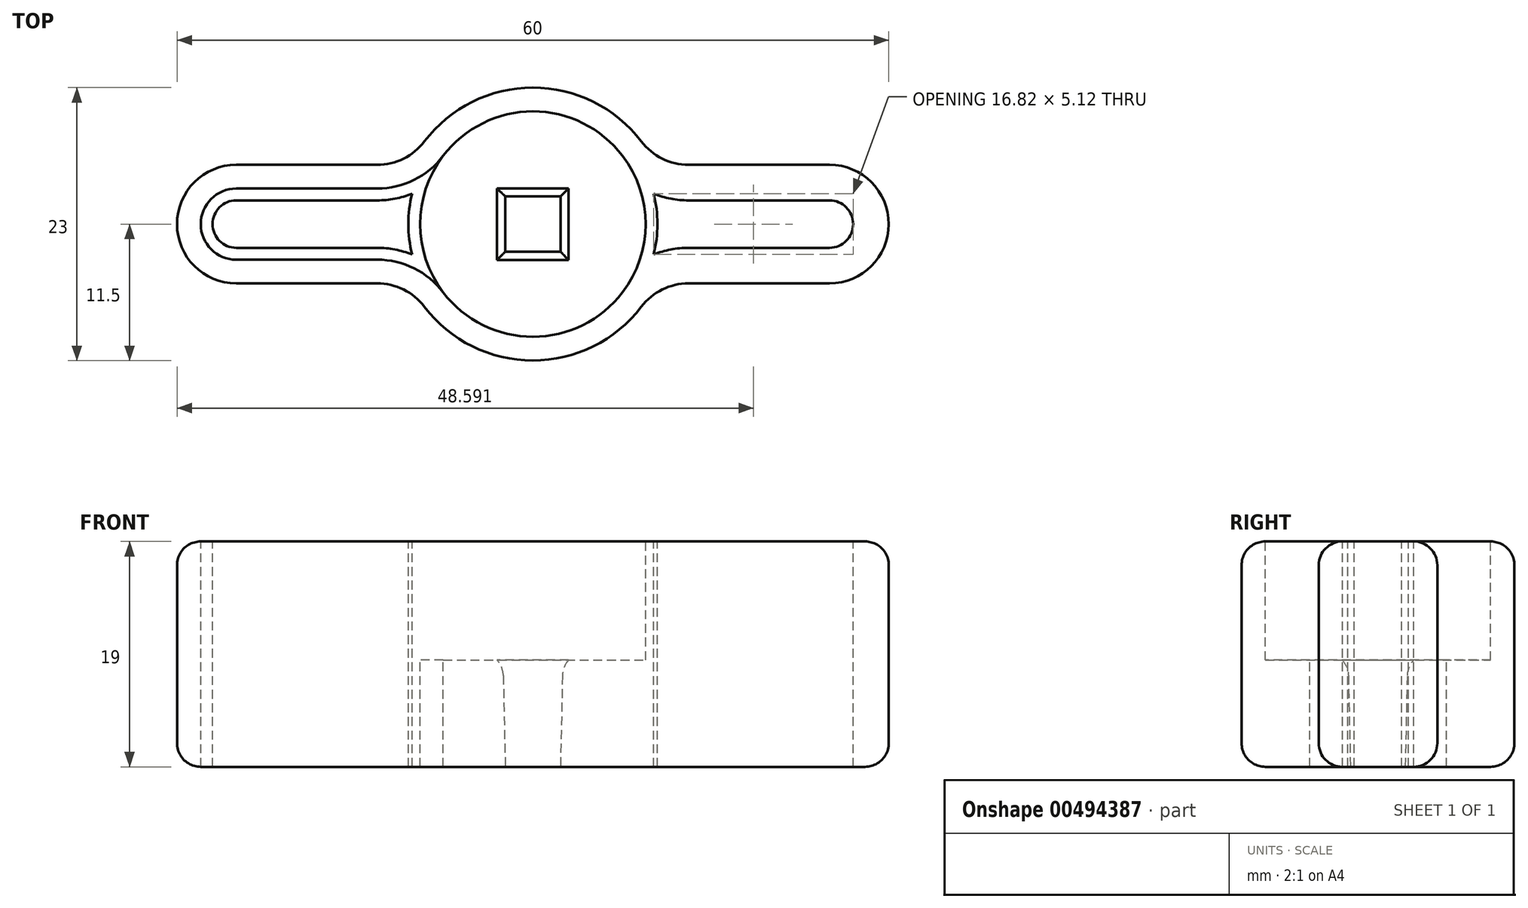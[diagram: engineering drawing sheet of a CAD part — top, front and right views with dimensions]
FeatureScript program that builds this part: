
annotation { "Feature Type Name" : "Feature", "Feature Type Description" : "" }
export const myFeature = defineFeature(function(context is Context, id is Id, definition is map)
    precondition{}
    {
        {
            var Q0;
            Q0=qCreatedBy(makeId("Top.planeOp"),FACE);
            var sketch = newSketch(context, id + "F0", { "sketchPlane" : qUnion([Q0])});
            skCircle(sketch, "E0", {"center": v(0, 0) * mm, "radius": 11.5 * mm});
            skLineSegment(sketch, "E1.bottom", {"start": v(2.32, 2.33) * mm, "end": v(-2.33, 2.33) * mm});
            skLineSegment(sketch, "E1.top", {"start": v(2.32, -2.33) * mm, "end": v(-2.33, -2.33) * mm});
            skLineSegment(sketch, "E1.left", {"start": v(2.32, 2.33) * mm, "end": v(2.32, -2.33) * mm});
            skLineSegment(sketch, "E1.right", {"start": v(-2.33, 2.33) * mm, "end": v(-2.33, -2.33) * mm});
            skLineSegment(sketch, "E2.bottom", {"start": v(30, 5) * mm, "end": v(-30, 5) * mm});
            skLineSegment(sketch, "E2.top", {"start": v(30, -5) * mm, "end": v(-30, -5) * mm});
            skLineSegment(sketch, "E2.left", {"start": v(30, 5) * mm, "end": v(30, -5) * mm});
            skLineSegment(sketch, "E2.right", {"start": v(-30, 5) * mm, "end": v(-30, -5) * mm});
            skSolve(sketch);
        }
        {
            var Q0;
            Q0=makeQuery(id+"F0.imprint","IMPRINT",FACE,{"disambiguationData":[TD([[makeQuery(id+"F0.imprint","IMPRINT",EDGE,{"derivedFrom":sQuery(id+"F0.wireOp",EDGE,"E0")}),1.0]])]});
            var Q1;
            {var subQ5=sQuery(id+"F0.wireOp",EDGE,"E2.right");Q1=makeQuery(id+"F0.imprint","IMPRINT",FACE,{"disambiguationData":[TD([[makeQuery(id+"F0.imprint","IMPRINT",EDGE,{"derivedFrom":subQ5}),1.0]])]});}
            var Q2;
            {var subQ5=sQuery(id+"F0.wireOp",EDGE,"E2.left");Q2=makeQuery(id+"F0.imprint","IMPRINT",FACE,{"disambiguationData":[TD([[makeQuery(id+"F0.imprint","IMPRINT",EDGE,{"derivedFrom":subQ5}),-1.0]])]});}
            extrude(context, id + "F1", {"entities" : qUnion([Q0, Q1, Q2]), "depth" : 19 * mm, "offsetDistance" : 25 * mm});
        }
        {
            var Q0;
            Q0=makeQuery(id+"F1.opExtrude","CAP_FACE",FACE,{"disambiguationData":[OSD([sQuery(id+"F0.wireOp",EDGE,"E0"),sQuery(id+"F0.wireOp",EDGE,"E1.bottom"),sQuery(id+"F0.wireOp",EDGE,"E1.top"),sQuery(id+"F0.wireOp",EDGE,"E1.left"),sQuery(id+"F0.wireOp",EDGE,"E1.right"),sQuery(id+"F0.wireOp",EDGE,"E2.bottom"),sQuery(id+"F0.wireOp",EDGE,"E2.top"),sQuery(id+"F0.wireOp",EDGE,"E2.left"),sQuery(id+"F0.wireOp",EDGE,"E2.right")])],"isStart":false});
            var sketch = newSketch(context, id + "F2", { "sketchPlane" : qUnion([Q0])});
            skCircle(sketch, "E3", {"center": v(0, 0) * mm, "radius": 9.5 * mm});
            skSolve(sketch);
        }
        {
            var Q0;
            Q0 = qSketchRegion(id + "F2", true);
            extrude(context, id + "F3", {"entities" : qUnion([Q0]), "operationType" : NewBodyOperationType.REMOVE, "oppositeDirection" : true, "depth" : 10 * mm, "offsetDistance" : 25 * mm});
        }
        {
            var Q0;
            Q0=makeQuery(id+"F3.boolean.opBoolean","INTERSECT",EDGE,{"derivedFrom":[makeQuery(id+"F1.opExtrude","SWEPT_FACE",FACE,{"disambiguationData":[OSD([sQuery(id+"F0.wireOp",EDGE,"E1.top")])]}),makeQuery(id+"F3.opExtrude","CAP_FACE",FACE,{"disambiguationData":[OSD([sQuery(id+"F2.wireOp",EDGE,"E3")])],"isStart":false})]});
            var Q1;
            Q1=makeQuery(id+"F3.boolean.opBoolean","INTERSECT",EDGE,{"derivedFrom":[makeQuery(id+"F1.opExtrude","SWEPT_FACE",FACE,{"disambiguationData":[OSD([sQuery(id+"F0.wireOp",EDGE,"E1.left")])]}),makeQuery(id+"F3.opExtrude","CAP_FACE",FACE,{"disambiguationData":[OSD([sQuery(id+"F2.wireOp",EDGE,"E3")])],"isStart":false})]});
            var Q2;
            Q2=makeQuery(id+"F3.boolean.opBoolean","INTERSECT",EDGE,{"derivedFrom":[makeQuery(id+"F1.opExtrude","SWEPT_FACE",FACE,{"disambiguationData":[OSD([sQuery(id+"F0.wireOp",EDGE,"E1.bottom")])]}),makeQuery(id+"F3.opExtrude","CAP_FACE",FACE,{"disambiguationData":[OSD([sQuery(id+"F2.wireOp",EDGE,"E3")])],"isStart":false})]});
            var Q3;
            Q3=makeQuery(id+"F3.boolean.opBoolean","INTERSECT",EDGE,{"derivedFrom":[makeQuery(id+"F1.opExtrude","SWEPT_FACE",FACE,{"disambiguationData":[OSD([sQuery(id+"F0.wireOp",EDGE,"E1.right")])]}),makeQuery(id+"F3.opExtrude","CAP_FACE",FACE,{"disambiguationData":[OSD([sQuery(id+"F2.wireOp",EDGE,"E3")])],"isStart":false})]});
            chamfer(context, id + "F4", {"entities" : qUnion([Q0, Q1, Q2, Q3]), "chamferType" : ChamferType.TWO_OFFSETS, "width1" : 9 * mm, "oppositeDirection" : true, "width2" : 0.2 * mm, "tangentPropagation" : true});
        }
        {
            var Q0;
            {var subQ0=sQuery(id+"F0.wireOp",EDGE,"E2.bottom");var subQ1=sQuery(id+"F0.wireOp",EDGE,"E0");Q0=makeQuery(id+"F1.opExtrude","SWEPT_EDGE",EDGE,{"disambiguationData":[OSD([subQ1,subQ0]),TDD([makeQuery(id+"F0.imprint","INTERSECT",VERTEX,{"disambiguationData":[OD(0.0)],"derivedFrom":[subQ1,subQ0]})])]});}
            var Q1;
            {var subQ0=sQuery(id+"F0.wireOp",EDGE,"E2.bottom");var subQ1=sQuery(id+"F0.wireOp",EDGE,"E0");Q1=makeQuery(id+"F1.opExtrude","SWEPT_EDGE",EDGE,{"disambiguationData":[OSD([subQ1,subQ0]),TDD([makeQuery(id+"F0.imprint","INTERSECT",VERTEX,{"disambiguationData":[OD(1.0)],"derivedFrom":[subQ1,subQ0]})])]});}
            var Q2;
            Q2=makeQuery(id+"F1.opExtrude","SWEPT_EDGE",EDGE,{"disambiguationData":[OSD([sQuery(id+"F0.wireOp",EDGE,"E2.bottom"),sQuery(id+"F0.wireOp",EDGE,"E2.right")])]});
            var Q3;
            Q3=makeQuery(id+"F1.opExtrude","SWEPT_EDGE",EDGE,{"disambiguationData":[OSD([sQuery(id+"F0.wireOp",EDGE,"E2.top"),sQuery(id+"F0.wireOp",EDGE,"E2.right")])]});
            var Q4;
            {var subQ0=sQuery(id+"F0.wireOp",EDGE,"E2.top");var subQ1=sQuery(id+"F0.wireOp",EDGE,"E0");Q4=makeQuery(id+"F1.opExtrude","SWEPT_EDGE",EDGE,{"disambiguationData":[OSD([subQ1,subQ0]),TDD([makeQuery(id+"F0.imprint","INTERSECT",VERTEX,{"disambiguationData":[OD(0.0)],"derivedFrom":[subQ1,subQ0]})])]});}
            var Q5;
            {var subQ0=sQuery(id+"F0.wireOp",EDGE,"E2.top");var subQ1=sQuery(id+"F0.wireOp",EDGE,"E0");Q5=makeQuery(id+"F1.opExtrude","SWEPT_EDGE",EDGE,{"disambiguationData":[OSD([subQ1,subQ0]),TDD([makeQuery(id+"F0.imprint","INTERSECT",VERTEX,{"disambiguationData":[OD(1.0)],"derivedFrom":[subQ1,subQ0]})])]});}
            var Q6;
            Q6=makeQuery(id+"F1.opExtrude","SWEPT_EDGE",EDGE,{"disambiguationData":[OSD([sQuery(id+"F0.wireOp",EDGE,"E2.top"),sQuery(id+"F0.wireOp",EDGE,"E2.left")])]});
            var Q7;
            Q7=makeQuery(id+"F1.opExtrude","SWEPT_EDGE",EDGE,{"disambiguationData":[OSD([sQuery(id+"F0.wireOp",EDGE,"E2.bottom"),sQuery(id+"F0.wireOp",EDGE,"E2.left")])]});
            fillet(context, id + "F5", {"entities" : qUnion([Q0, Q1, Q2, Q3, Q4, Q5, Q6, Q7]), "radius" : 5 * mm, "tangentPropagation" : true, "allowEdgeOverflow" : false});
        }
        {
            var Q0;
            {var subQ0=sQuery(id+"F0.wireOp",EDGE,"E2.bottom");Q0=makeQuery(id+"F1.opExtrude","CAP_EDGE",EDGE,{"disambiguationData":[OSD([subQ0]),TDD([makeQuery(id+"F0.imprint","IMPRINT",EDGE,{"disambiguationData":[TD([[makeQuery(id+"F0.imprint","INTERSECT",VERTEX,{"derivedFrom":[subQ0,sQuery(id+"F0.wireOp",EDGE,"E2.right")]}),1.0]])],"derivedFrom":subQ0})])],"isStart":true});}
            var Q1;
            {var subQ0=sQuery(id+"F0.wireOp",EDGE,"E2.bottom");Q1=makeQuery(id+"F1.opExtrude","CAP_EDGE",EDGE,{"disambiguationData":[OSD([subQ0]),TDD([makeQuery(id+"F0.imprint","IMPRINT",EDGE,{"disambiguationData":[TD([[makeQuery(id+"F0.imprint","INTERSECT",VERTEX,{"derivedFrom":[subQ0,sQuery(id+"F0.wireOp",EDGE,"E2.right")]}),1.0]])],"derivedFrom":subQ0})])],"isStart":false});}
            fillet(context, id + "F6", {"entities" : qUnion([Q0, Q1]), "radius" : 2 * mm, "tangentPropagation" : true, "allowEdgeOverflow" : false});
        }
        {
            var Q0;
            {var subQ0=makeQuery(id+"F3.opExtrude","CAP_FACE",FACE,{"disambiguationData":[OSD([sQuery(id+"F2.wireOp",EDGE,"E3")])],"isStart":false});Q0=makeQuery(id+"F4.opChamfer","BLEND_EDGE",EDGE,{"blendedFrom":[makeQuery(id+"F3.boolean.opBoolean","INTERSECT",EDGE,{"derivedFrom":[makeQuery(id+"F1.opExtrude","SWEPT_FACE",FACE,{"disambiguationData":[OSD([sQuery(id+"F0.wireOp",EDGE,"E1.bottom")])]}),subQ0]}),makeQuery(id+"F3.boolean.opBoolean","COPY",FACE,{"derivedFrom":subQ0})],"blendedInto":[makeQuery(id+"F3.boolean.opBoolean","COPY",FACE,{"derivedFrom":subQ0})]});}
            var Q1;
            {var subQ0=makeQuery(id+"F3.opExtrude","CAP_FACE",FACE,{"disambiguationData":[OSD([sQuery(id+"F2.wireOp",EDGE,"E3")])],"isStart":false});Q1=makeQuery(id+"F4.opChamfer","BLEND_EDGE",EDGE,{"blendedFrom":[makeQuery(id+"F3.boolean.opBoolean","INTERSECT",EDGE,{"derivedFrom":[makeQuery(id+"F1.opExtrude","SWEPT_FACE",FACE,{"disambiguationData":[OSD([sQuery(id+"F0.wireOp",EDGE,"E1.right")])]}),subQ0]}),makeQuery(id+"F3.boolean.opBoolean","COPY",FACE,{"derivedFrom":subQ0})],"blendedInto":[makeQuery(id+"F3.boolean.opBoolean","COPY",FACE,{"derivedFrom":subQ0})]});}
            var Q2;
            {var subQ0=makeQuery(id+"F3.opExtrude","CAP_FACE",FACE,{"disambiguationData":[OSD([sQuery(id+"F2.wireOp",EDGE,"E3")])],"isStart":false});Q2=makeQuery(id+"F4.opChamfer","BLEND_EDGE",EDGE,{"blendedFrom":[makeQuery(id+"F3.boolean.opBoolean","INTERSECT",EDGE,{"derivedFrom":[makeQuery(id+"F1.opExtrude","SWEPT_FACE",FACE,{"disambiguationData":[OSD([sQuery(id+"F0.wireOp",EDGE,"E1.left")])]}),subQ0]}),makeQuery(id+"F3.boolean.opBoolean","COPY",FACE,{"derivedFrom":subQ0})],"blendedInto":[makeQuery(id+"F3.boolean.opBoolean","COPY",FACE,{"derivedFrom":subQ0})]});}
            var Q3;
            {var subQ0=makeQuery(id+"F3.opExtrude","CAP_FACE",FACE,{"disambiguationData":[OSD([sQuery(id+"F2.wireOp",EDGE,"E3")])],"isStart":false});Q3=makeQuery(id+"F4.opChamfer","BLEND_EDGE",EDGE,{"blendedFrom":[makeQuery(id+"F3.boolean.opBoolean","INTERSECT",EDGE,{"derivedFrom":[makeQuery(id+"F1.opExtrude","SWEPT_FACE",FACE,{"disambiguationData":[OSD([sQuery(id+"F0.wireOp",EDGE,"E1.top")])]}),subQ0]}),makeQuery(id+"F3.boolean.opBoolean","COPY",FACE,{"derivedFrom":subQ0})],"blendedInto":[makeQuery(id+"F3.boolean.opBoolean","COPY",FACE,{"derivedFrom":subQ0})]});}
            chamfer(context, id + "F7", {"entities" : qUnion([Q0, Q1, Q2, Q3]), "width" : 0.5 * mm, "tangentPropagation" : true});
        }
        {
            var Q0;
            {var subQ0=sQuery(id+"F2.wireOp",EDGE,"E3");var subQ1=sQuery(id+"F0.wireOp",EDGE,"E1.bottom");var subQ2=makeQuery(id+"F3.opExtrude","CAP_FACE",FACE,{"disambiguationData":[OSD([subQ0])],"isStart":false});Q0=makeQuery(id+"F7.opChamfer","BLEND_EDGE",EDGE,{"blendedFrom":[makeQuery(id+"F4.opChamfer","BLEND_EDGE",EDGE,{"blendedFrom":[makeQuery(id+"F3.boolean.opBoolean","INTERSECT",EDGE,{"derivedFrom":[makeQuery(id+"F1.opExtrude","SWEPT_FACE",FACE,{"disambiguationData":[OSD([subQ1])]}),subQ2]}),makeQuery(id+"F3.boolean.opBoolean","COPY",FACE,{"derivedFrom":subQ2})],"blendedInto":[makeQuery(id+"F3.boolean.opBoolean","COPY",FACE,{"derivedFrom":subQ2})]}),makeQuery(id+"F4.opChamfer","BLEND_FACE",FACE,{"disambiguationData":[OSD([subQ1,subQ0])]})],"blendedInto":[makeQuery(id+"F4.opChamfer","BLEND_FACE",FACE,{"disambiguationData":[OSD([subQ1,subQ0])]})]});}
            var Q1;
            {var subQ0=sQuery(id+"F2.wireOp",EDGE,"E3");var subQ1=sQuery(id+"F0.wireOp",EDGE,"E1.right");var subQ2=makeQuery(id+"F3.opExtrude","CAP_FACE",FACE,{"disambiguationData":[OSD([subQ0])],"isStart":false});Q1=makeQuery(id+"F7.opChamfer","BLEND_EDGE",EDGE,{"blendedFrom":[makeQuery(id+"F4.opChamfer","BLEND_EDGE",EDGE,{"blendedFrom":[makeQuery(id+"F3.boolean.opBoolean","INTERSECT",EDGE,{"derivedFrom":[makeQuery(id+"F1.opExtrude","SWEPT_FACE",FACE,{"disambiguationData":[OSD([subQ1])]}),subQ2]}),makeQuery(id+"F3.boolean.opBoolean","COPY",FACE,{"derivedFrom":subQ2})],"blendedInto":[makeQuery(id+"F3.boolean.opBoolean","COPY",FACE,{"derivedFrom":subQ2})]}),makeQuery(id+"F4.opChamfer","BLEND_FACE",FACE,{"disambiguationData":[OSD([subQ1,subQ0])]})],"blendedInto":[makeQuery(id+"F4.opChamfer","BLEND_FACE",FACE,{"disambiguationData":[OSD([subQ1,subQ0])]})]});}
            var Q2;
            {var subQ0=sQuery(id+"F2.wireOp",EDGE,"E3");var subQ1=sQuery(id+"F0.wireOp",EDGE,"E1.top");var subQ2=makeQuery(id+"F3.opExtrude","CAP_FACE",FACE,{"disambiguationData":[OSD([subQ0])],"isStart":false});Q2=makeQuery(id+"F7.opChamfer","BLEND_EDGE",EDGE,{"blendedFrom":[makeQuery(id+"F4.opChamfer","BLEND_EDGE",EDGE,{"blendedFrom":[makeQuery(id+"F3.boolean.opBoolean","INTERSECT",EDGE,{"derivedFrom":[makeQuery(id+"F1.opExtrude","SWEPT_FACE",FACE,{"disambiguationData":[OSD([subQ1])]}),subQ2]}),makeQuery(id+"F3.boolean.opBoolean","COPY",FACE,{"derivedFrom":subQ2})],"blendedInto":[makeQuery(id+"F3.boolean.opBoolean","COPY",FACE,{"derivedFrom":subQ2})]}),makeQuery(id+"F4.opChamfer","BLEND_FACE",FACE,{"disambiguationData":[OSD([subQ1,subQ0])]})],"blendedInto":[makeQuery(id+"F4.opChamfer","BLEND_FACE",FACE,{"disambiguationData":[OSD([subQ1,subQ0])]})]});}
            var Q3;
            {var subQ0=sQuery(id+"F2.wireOp",EDGE,"E3");var subQ1=sQuery(id+"F0.wireOp",EDGE,"E1.left");var subQ2=makeQuery(id+"F3.opExtrude","CAP_FACE",FACE,{"disambiguationData":[OSD([subQ0])],"isStart":false});Q3=makeQuery(id+"F7.opChamfer","BLEND_EDGE",EDGE,{"blendedFrom":[makeQuery(id+"F4.opChamfer","BLEND_EDGE",EDGE,{"blendedFrom":[makeQuery(id+"F3.boolean.opBoolean","INTERSECT",EDGE,{"derivedFrom":[makeQuery(id+"F1.opExtrude","SWEPT_FACE",FACE,{"disambiguationData":[OSD([subQ1])]}),subQ2]}),makeQuery(id+"F3.boolean.opBoolean","COPY",FACE,{"derivedFrom":subQ2})],"blendedInto":[makeQuery(id+"F3.boolean.opBoolean","COPY",FACE,{"derivedFrom":subQ2})]}),makeQuery(id+"F4.opChamfer","BLEND_FACE",FACE,{"disambiguationData":[OSD([subQ1,subQ0])]})],"blendedInto":[makeQuery(id+"F4.opChamfer","BLEND_FACE",FACE,{"disambiguationData":[OSD([subQ1,subQ0])]})]});}
            fillet(context, id + "F8", {"entities" : qUnion([Q0, Q1, Q2, Q3]), "radius" : 2 * mm, "tangentPropagation" : true, "allowEdgeOverflow" : false});
        }
        {
            var Q0;
            Q0=makeQuery(id+"F6.opFillet","SPLIT",FACE,{"disambiguationData":[OD(1.0)],"derivedFrom":makeQuery(id+"F1.opExtrude","CAP_FACE",FACE,{"disambiguationData":[OSD([sQuery(id+"F0.wireOp",EDGE,"E0"),sQuery(id+"F0.wireOp",EDGE,"E1.bottom"),sQuery(id+"F0.wireOp",EDGE,"E1.top"),sQuery(id+"F0.wireOp",EDGE,"E1.left"),sQuery(id+"F0.wireOp",EDGE,"E1.right"),sQuery(id+"F0.wireOp",EDGE,"E2.bottom"),sQuery(id+"F0.wireOp",EDGE,"E2.top"),sQuery(id+"F0.wireOp",EDGE,"E2.left"),sQuery(id+"F0.wireOp",EDGE,"E2.right")])],"isStart":false})});
            var sketch = newSketch(context, id + "F9", { "sketchPlane" : qUnion([Q0])});
            skArc(sketch, "E4.0.0", {"start": v(7.56, 5.76) * mm, "mid": v(9.5, 0) * mm, "end": v(7.56, -5.76) * mm});
            skArc(sketch, "E4.0.1", {"start": v(7.56, -5.76) * mm, "mid": v(10.02, -3.73) * mm, "end": v(13.12, -3) * mm});
            skLineSegment(sketch, "E4.0.2", {"start": v(13.12, -3) * mm, "end": v(25, -3) * mm});
            skArc(sketch, "E4.0.3", {"start": v(25, -3) * mm, "mid": v(28, 0) * mm, "end": v(25, 3) * mm});
            skLineSegment(sketch, "E4.0.4", {"start": v(25, 3) * mm, "end": v(13.12, 3) * mm});
            skArc(sketch, "E4.0.5", {"start": v(13.12, 3) * mm, "mid": v(10.02, 3.73) * mm, "end": v(7.56, 5.76) * mm});
            skLineSegment(sketch, "E5.0", {"start": v(25, 2) * mm, "end": v(13.12, 2) * mm});
            skArc(sketch, "E5.1", {"start": v(10.18, 2.56) * mm, "mid": v(10.5, 0) * mm, "end": v(10.18, -2.56) * mm});
            skArc(sketch, "E5.2", {"start": v(10.18, -2.56) * mm, "mid": v(11.63, -2.14) * mm, "end": v(13.12, -2) * mm});
            skArc(sketch, "E5.3", {"start": v(13.12, 2) * mm, "mid": v(11.63, 2.14) * mm, "end": v(10.18, 2.56) * mm});
            skLineSegment(sketch, "E5.4", {"start": v(13.12, -2) * mm, "end": v(25, -2) * mm});
            skArc(sketch, "E5.5", {"start": v(25, -2) * mm, "mid": v(27, 0) * mm, "end": v(25, 2) * mm});
            skArc(sketch, "E6.MirrorCS", {"start": v(-25, -2) * mm, "mid": v(-27, 0) * mm, "end": v(-25, 2) * mm});
            skArc(sketch, "E7.MirrorCS", {"start": v(-13.12, 2) * mm, "mid": v(-11.63, 2.14) * mm, "end": v(-10.18, 2.56) * mm});
            skArc(sketch, "E8.MirrorCS", {"start": v(-10.18, 2.56) * mm, "mid": v(-10.5, 0) * mm, "end": v(-10.18, -2.56) * mm});
            skArc(sketch, "E9.MirrorCS", {"start": v(-10.18, -2.56) * mm, "mid": v(-11.63, -2.14) * mm, "end": v(-13.12, -2) * mm});
            skLineSegment(sketch, "E10.MirrorCS", {"start": v(-25, 2) * mm, "end": v(-13.12, 2) * mm});
            skLineSegment(sketch, "E11.MirrorCS", {"start": v(-13.12, -2) * mm, "end": v(-25, -2) * mm});
            skSolve(sketch);
        }
        {
            var Q0;
            Q0=makeQuery(id+"F9.imprint","IMPRINT",FACE,{"disambiguationData":[TD([[makeQuery(id+"F9.imprint","IMPRINT",EDGE,{"derivedFrom":sQuery(id+"F9.wireOp",EDGE,"E6.MirrorCS")}),-1.0]])]});
            var Q1;
            Q1=makeQuery(id+"F9.imprint","IMPRINT",FACE,{"disambiguationData":[TD([[makeQuery(id+"F9.imprint","IMPRINT",EDGE,{"derivedFrom":sQuery(id+"F9.wireOp",EDGE,"E5.0")}),1.0]])]});
            extrude(context, id + "F10", {"entities" : qUnion([Q0, Q1]), "operationType" : NewBodyOperationType.REMOVE, "oppositeDirection" : true, "depth" : 25 * mm, "offsetDistance" : 25 * mm});
        }
    });
